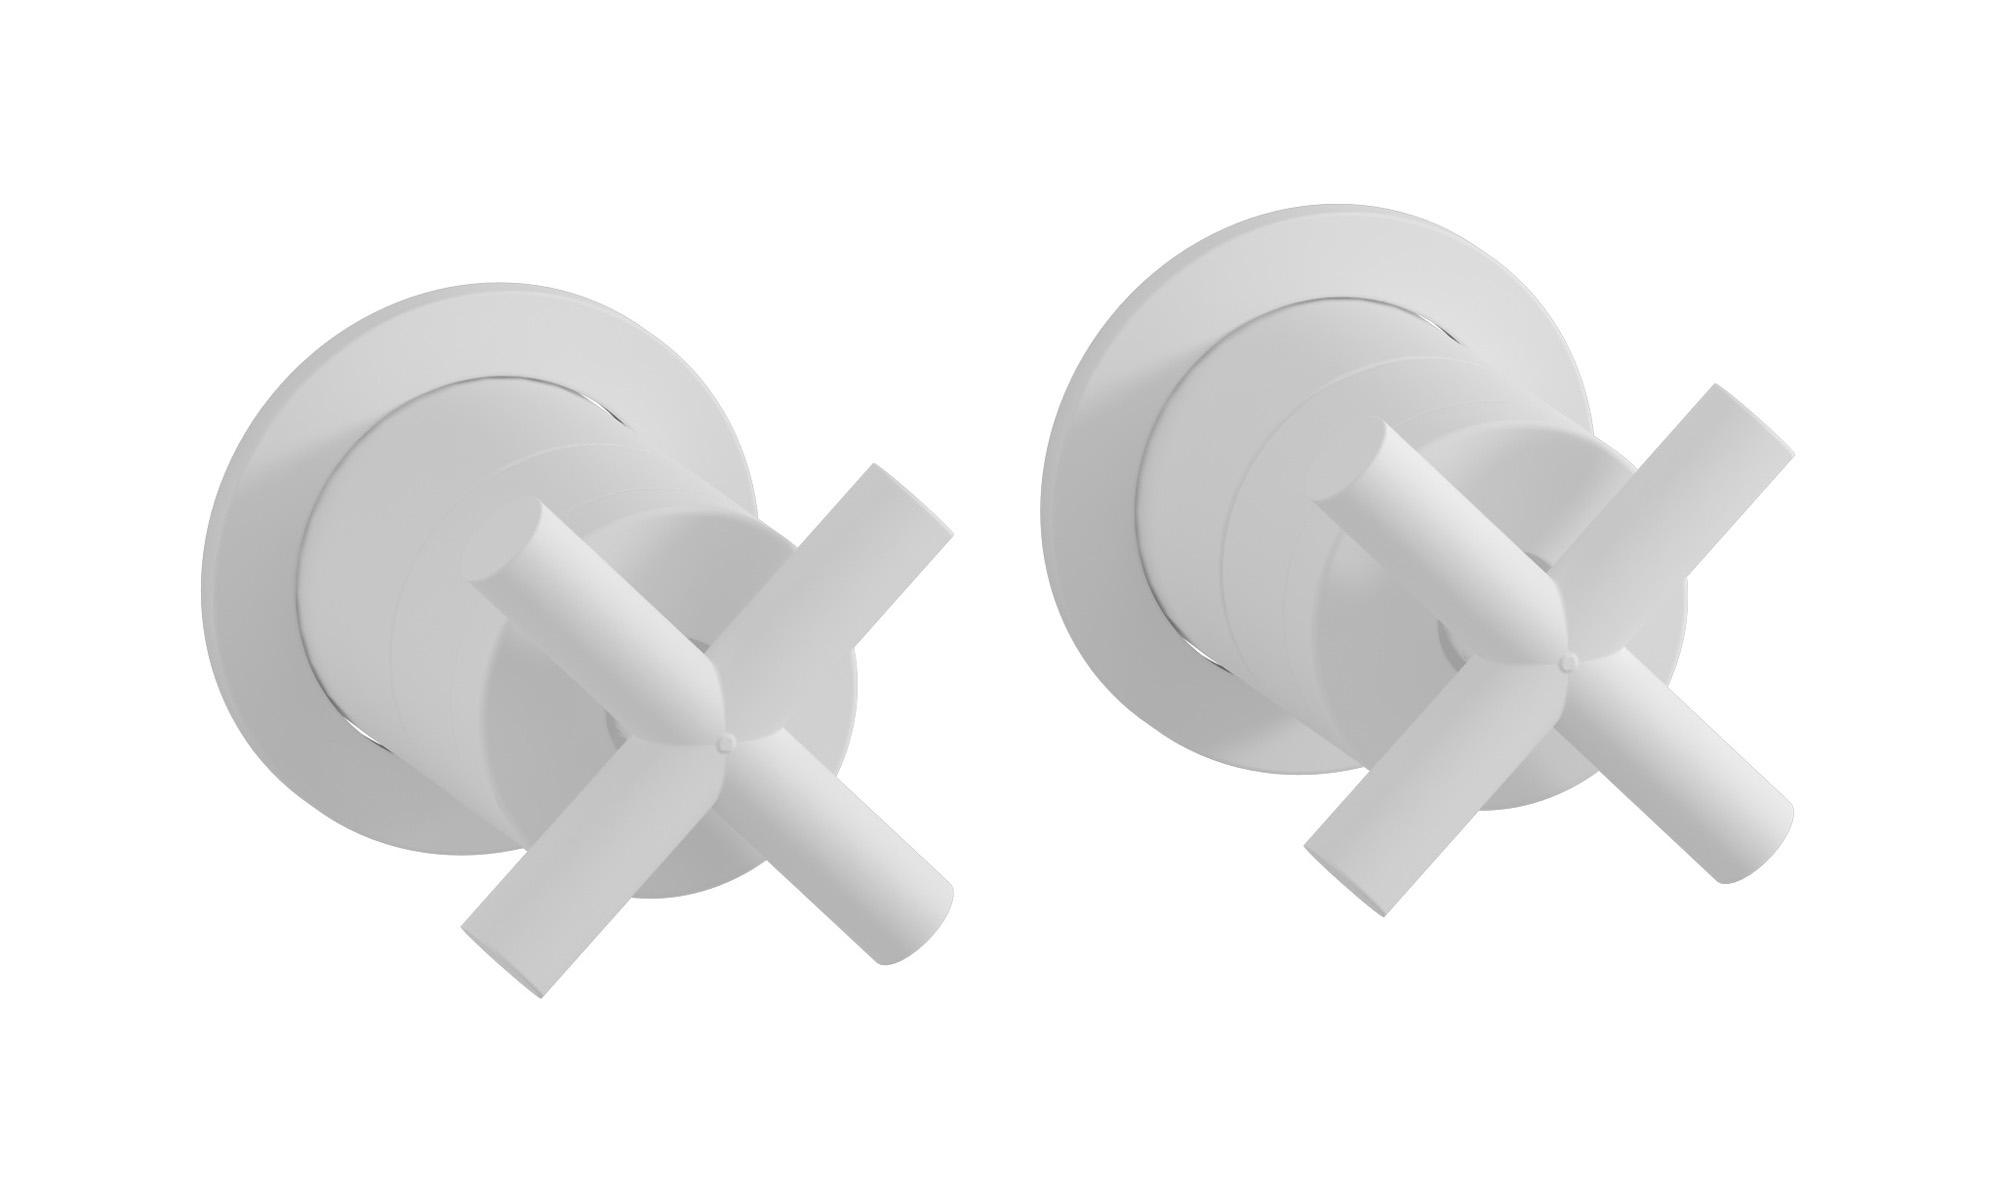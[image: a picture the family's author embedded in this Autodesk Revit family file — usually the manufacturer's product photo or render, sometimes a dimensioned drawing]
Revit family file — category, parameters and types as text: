
# Revit family: WO400
name_source: partatom
category: Apparecchi idraulici
units: mm (PartAtom-declared; Revit-internal decimal feet)

## family parameters
Basato su piano di lavoro = No
Condiviso = No
Mantieni orientamento annotazione = No
Numero OmniClass = 23.45.55.17
Punto di calcolo locali = No
Quota connettore circolare = Usa diametro
Sempre verticale = Sì
Taglio con vuoti quando caricato = No
Tipo di parte = Normale
Titolo OmniClass = Mixing Faucets

## types (5) — shared parameters
Cold water inlet = 10 mm  [stored 0.0328084 ft]
Commenti sul tipo = Shower mixer
Connessione CW = No
Connessione HW = No
Connessione di scarico = No
Connessione di ventilazione = No
Descrizione = Two holes wall mounted shower
Hot water inlet = 10 mm  [stored 0.0328084 ft]
Produttore = IB Rubinetterie S.p.A.
URL = https://www.weareib.it
zero-valued in all types: Prospetto di default

## per-type parameters (varying)
| type | Finishes surface | Immagine tipo | Modello |
| Chrome | IB_Chrome | WO400CC.jpg | WO400CC |
| Brushed nickel | IB_Brushed nickel | WO400SS.jpg | WO400SS |
| Matt black | IB_matt black | WO400NP.jpg | WO400NP |
| Matt white | IB_matt white | WO400BO.jpg | WO400BO |
| Gold | IB_gold | WO400OO.jpg | WO400OO |

note: [stored X ft] marks values corroborated as IEEE doubles in the binary element streams (Revit-internal decimal feet)
